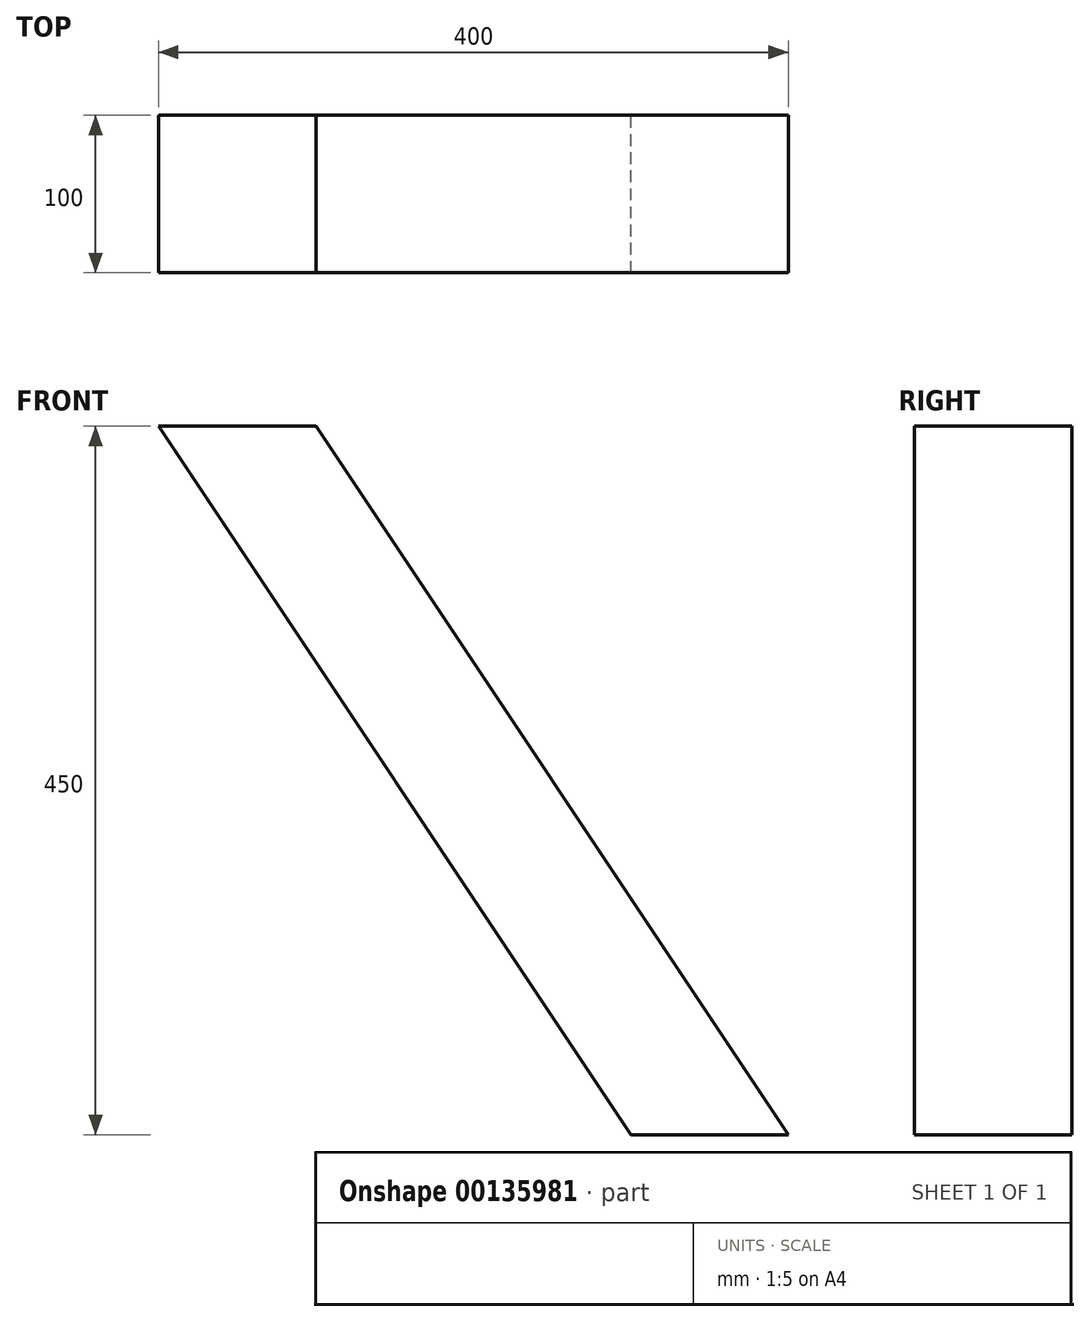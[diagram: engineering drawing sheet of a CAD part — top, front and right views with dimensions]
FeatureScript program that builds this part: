
annotation { "Feature Type Name" : "Feature", "Feature Type Description" : "" }
export const myFeature = defineFeature(function(context is Context, id is Id, definition is map)
    precondition{}
    {
        {
            var Q0;
            Q0=qCreatedBy(makeId("Front.planeOp"),FACE);
            var sketch = newSketch(context, id + "F0", { "sketchPlane" : qUnion([Q0])});
            skLineSegment(sketch, "E0", {"start": v(0, 0) * mm, "end": v(100, 0) * mm});
            skLineSegment(sketch, "E1", {"start": v(100, 0) * mm, "end": v(400, -450) * mm});
            skLineSegment(sketch, "E2", {"start": v(400, -450) * mm, "end": v(300, -450) * mm});
            skLineSegment(sketch, "E3", {"start": v(300, -450) * mm, "end": v(0, 0) * mm});
            skSolve(sketch);
        }
        {
            var Q0;
            Q0=makeQuery(id+"F0.imprint","IMPRINT",FACE,{"disambiguationData":[TD([[makeQuery(id+"F0.imprint","IMPRINT",EDGE,{"derivedFrom":sQuery(id+"F0.wireOp",EDGE,"E0")}),-1.0]])]});
            extrude(context, id + "F1", {"entities" : qUnion([Q0]), "endBound" : BoundingType.SYMMETRIC, "depth" : 100 * mm});
        }
    });
